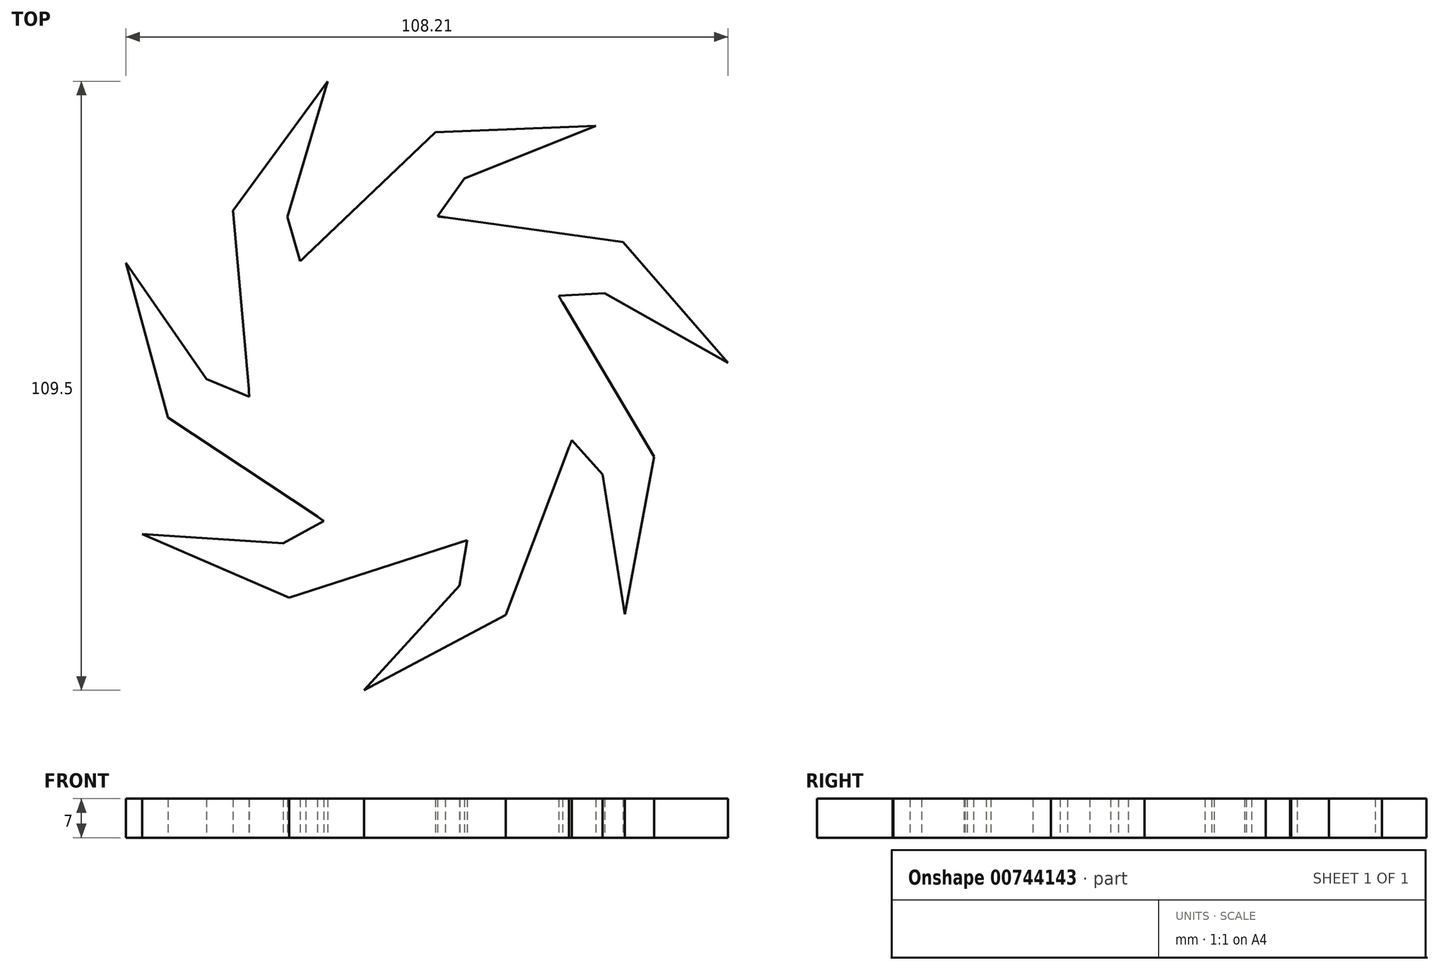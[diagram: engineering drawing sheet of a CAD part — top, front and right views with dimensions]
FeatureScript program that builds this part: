
annotation { "Feature Type Name" : "Feature", "Feature Type Description" : "" }
export const myFeature = defineFeature(function(context is Context, id is Id, definition is map)
    precondition{}
    {
        {
            var Q0;
            Q0=qCreatedBy(makeId("Top.planeOp"),FACE);
            var sketch = newSketch(context, id + "F0", { "sketchPlane" : qUnion([Q0])});
            skCircle(sketch, "E0", {"center": v(0, 0) * mm, "radius": 30 * mm});
            skLineSegment(sketch, "E1", {"start": v(5.36, 29.52) * mm, "end": v(37.29, 25.13) * mm});
            skLineSegment(sketch, "E2", {"start": v(37.29, 25.13) * mm, "end": v(56.16, 3.36) * mm});
            skLineSegment(sketch, "E3", {"start": v(56.16, 3.36) * mm, "end": v(34.02, 15.88) * mm});
            skLineSegment(sketch, "E4", {"start": v(34.02, 15.88) * mm, "end": v(-3, 13.88) * mm});
            skLineSegment(sketch, "E5.1.0", {"start": v(-19.74, 22.6) * mm, "end": v(3.6, 44.82) * mm});
            skLineSegment(sketch, "E5.1.1", {"start": v(3.6, 44.82) * mm, "end": v(32.4, 46) * mm});
            skLineSegment(sketch, "E5.1.2", {"start": v(32.4, 46) * mm, "end": v(8.8, 36.5) * mm});
            skLineSegment(sketch, "E5.1.3", {"start": v(8.8, 36.5) * mm, "end": v(-12.72, 6.31) * mm});
            skLineSegment(sketch, "E5.2.0", {"start": v(-29.97, -1.34) * mm, "end": v(-32.8, 30.76) * mm});
            skLineSegment(sketch, "E5.2.1", {"start": v(-32.8, 30.76) * mm, "end": v(-15.77, 54) * mm});
            skLineSegment(sketch, "E5.2.2", {"start": v(-15.77, 54) * mm, "end": v(-23.05, 29.64) * mm});
            skLineSegment(sketch, "E5.2.3", {"start": v(-23.05, 29.64) * mm, "end": v(-12.87, -6) * mm});
            skLineSegment(sketch, "E5.3.0", {"start": v(-17.64, -24.27) * mm, "end": v(-44.5, -6.46) * mm});
            skLineSegment(sketch, "E5.3.1", {"start": v(-44.5, -6.46) * mm, "end": v(-52.05, 21.34) * mm});
            skLineSegment(sketch, "E5.3.2", {"start": v(-52.05, 21.34) * mm, "end": v(-37.54, 0.46) * mm});
            skLineSegment(sketch, "E5.3.3", {"start": v(-37.54, 0.46) * mm, "end": v(-3.33, -13.8) * mm});
            skLineSegment(sketch, "E5.4.0", {"start": v(7.98, -28.92) * mm, "end": v(-22.7, -38.82) * mm});
            skLineSegment(sketch, "E5.4.1", {"start": v(-22.7, -38.82) * mm, "end": v(-49.14, -27.4) * mm});
            skLineSegment(sketch, "E5.4.2", {"start": v(-49.14, -27.4) * mm, "end": v(-23.76, -29.07) * mm});
            skLineSegment(sketch, "E5.4.3", {"start": v(-23.76, -29.07) * mm, "end": v(8.72, -11.2) * mm});
            skLineSegment(sketch, "E5.5.0", {"start": v(27.58, -11.8) * mm, "end": v(16.2, -41.95) * mm});
            skLineSegment(sketch, "E5.5.1", {"start": v(16.2, -41.95) * mm, "end": v(-9.22, -55.5) * mm});
            skLineSegment(sketch, "E5.5.2", {"start": v(-9.22, -55.5) * mm, "end": v(7.9, -36.7) * mm});
            skLineSegment(sketch, "E5.5.3", {"start": v(7.9, -36.7) * mm, "end": v(14.2, -0.17) * mm});
            skLineSegment(sketch, "E5.6.0", {"start": v(26.42, 14.21) * mm, "end": v(42.9, -13.48) * mm});
            skLineSegment(sketch, "E5.6.1", {"start": v(42.9, -13.48) * mm, "end": v(37.64, -41.81) * mm});
            skLineSegment(sketch, "E5.6.2", {"start": v(37.64, -41.81) * mm, "end": v(33.63, -16.7) * mm});
            skLineSegment(sketch, "E5.6.3", {"start": v(33.63, -16.7) * mm, "end": v(8.99, 11) * mm});
            skSolve(sketch);
        }
        {
            var Q0;
            {var subQ1=sQuery(id+"F0.wireOp",EDGE,"E5.1.0");Q0=makeQuery(id+"F0.imprint","IMPRINT",FACE,{"disambiguationData":[TD([[makeQuery(id+"F0.imprint","IMPRINT",EDGE,{"derivedFrom":subQ1}),-1.0]])]});}
            var Q1;
            {var subQ0=sQuery(id+"F0.wireOp",EDGE,"E1");Q1=makeQuery(id+"F0.imprint","IMPRINT",FACE,{"disambiguationData":[TD([[makeQuery(id+"F0.imprint","IMPRINT",EDGE,{"derivedFrom":subQ0}),-1.0]])]});}
            var Q2;
            {var subQ1=sQuery(id+"F0.wireOp",EDGE,"E5.6.0");Q2=makeQuery(id+"F0.imprint","IMPRINT",FACE,{"disambiguationData":[TD([[makeQuery(id+"F0.imprint","IMPRINT",EDGE,{"derivedFrom":subQ1}),-1.0]])]});}
            var Q3;
            {var subQ0=sQuery(id+"F0.wireOp",EDGE,"E5.5.0");Q3=makeQuery(id+"F0.imprint","IMPRINT",FACE,{"disambiguationData":[TD([[makeQuery(id+"F0.imprint","IMPRINT",EDGE,{"derivedFrom":subQ0}),-1.0]])]});}
            var Q4;
            {var subQ1=sQuery(id+"F0.wireOp",EDGE,"E5.4.0");Q4=makeQuery(id+"F0.imprint","IMPRINT",FACE,{"disambiguationData":[TD([[makeQuery(id+"F0.imprint","IMPRINT",EDGE,{"derivedFrom":subQ1}),-1.0]])]});}
            var Q5;
            {var subQ1=sQuery(id+"F0.wireOp",EDGE,"E5.3.0");Q5=makeQuery(id+"F0.imprint","IMPRINT",FACE,{"disambiguationData":[TD([[makeQuery(id+"F0.imprint","IMPRINT",EDGE,{"derivedFrom":subQ1}),-1.0]])]});}
            var Q6;
            {var subQ0=sQuery(id+"F0.wireOp",EDGE,"E0");var subQ8=makeQuery(id+"F0.imprint","INTERSECT",VERTEX,{"derivedFrom":[subQ0,sQuery(id+"F0.wireOp",EDGE,"E5.6.0")]});Q6=makeQuery(id+"F0.imprint","IMPRINT",FACE,{"disambiguationData":[TD([[makeQuery(id+"F0.imprint","IMPRINT",EDGE,{"disambiguationData":[TD([[subQ8,-1.0]])],"derivedFrom":subQ0}),1.0]])]});}
            var Q7;
            {var subQ1=sQuery(id+"F0.wireOp",EDGE,"E5.2.0");Q7=makeQuery(id+"F0.imprint","IMPRINT",FACE,{"disambiguationData":[TD([[makeQuery(id+"F0.imprint","IMPRINT",EDGE,{"derivedFrom":subQ1}),-1.0]])]});}
            extrude(context, id + "F1", {"entities" : qUnion([Q0, Q1, Q2, Q3, Q4, Q5, Q6, Q7]), "depth" : 7 * mm, "offsetDistance" : 25 * mm});
        }
    });
